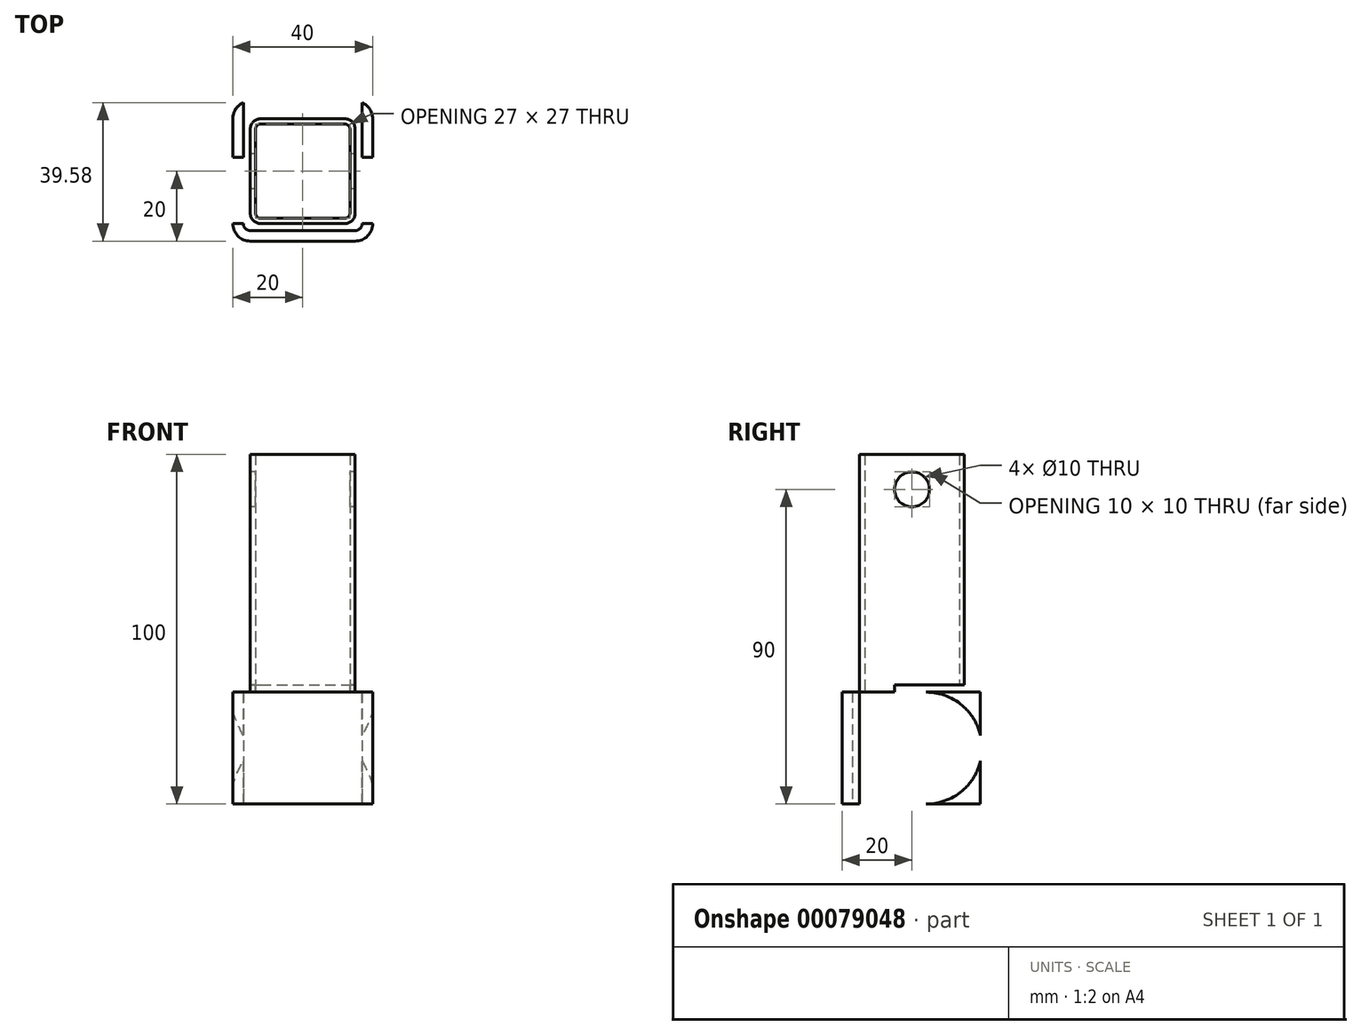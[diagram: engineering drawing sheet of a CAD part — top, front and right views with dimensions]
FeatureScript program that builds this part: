
annotation { "Feature Type Name" : "Feature", "Feature Type Description" : "" }
export const myFeature = defineFeature(function(context is Context, id is Id, definition is map)
    precondition{}
    {
        {
            var Q0;
            Q0=qCreatedBy(makeId("Top.planeOp"),FACE);
            var sketch = newSketch(context, id + "F0", { "sketchPlane" : qUnion([Q0])});
            skLineSegment(sketch, "E0.bottom", {"start": v(12, 15) * mm, "end": v(-12, 15) * mm});
            skLineSegment(sketch, "E0.top", {"start": v(12, -15) * mm, "end": v(-12, -15) * mm});
            skLineSegment(sketch, "E0.left", {"start": v(15, 12) * mm, "end": v(15, -12) * mm});
            skLineSegment(sketch, "E0.right", {"start": v(-15, 12) * mm, "end": v(-15, -12) * mm});
            skLineSegment(sketch, "E1", {"start": v(15, 15) * mm, "end": v(-15, -15) * mm, "construction": true});
            skPoint(sketch, "E2.visualSharp", {"position": v(15, 15) * mm});
            skArc(sketch, "E2.filletArc", {"start": v(15, 12) * mm, "mid": v(14.12, 14.12) * mm, "end": v(12, 15) * mm});
            skPoint(sketch, "E3.visualSharp", {"position": v(-15, 15) * mm});
            skArc(sketch, "E3.filletArc", {"start": v(-12, 15) * mm, "mid": v(-14.12, 14.12) * mm, "end": v(-15, 12) * mm});
            skPoint(sketch, "E4.visualSharp", {"position": v(-15, -15) * mm});
            skArc(sketch, "E4.filletArc", {"start": v(-15, -12) * mm, "mid": v(-14.12, -14.12) * mm, "end": v(-12, -15) * mm});
            skPoint(sketch, "E5.visualSharp", {"position": v(15, -15) * mm});
            skArc(sketch, "E5.filletArc", {"start": v(12, -15) * mm, "mid": v(14.12, -14.12) * mm, "end": v(15, -12) * mm});
            skArc(sketch, "E6.0", {"start": v(13.5, 12) * mm, "mid": v(13.06, 13.06) * mm, "end": v(12, 13.5) * mm});
            skLineSegment(sketch, "E6.1", {"start": v(12, 13.5) * mm, "end": v(-12, 13.5) * mm});
            skLineSegment(sketch, "E6.2", {"start": v(13.5, 12) * mm, "end": v(13.5, -12) * mm});
            skArc(sketch, "E6.3", {"start": v(-12, 13.5) * mm, "mid": v(-13.06, 13.06) * mm, "end": v(-13.5, 12) * mm});
            skArc(sketch, "E6.4", {"start": v(12, -13.5) * mm, "mid": v(13.06, -13.06) * mm, "end": v(13.5, -12) * mm});
            skLineSegment(sketch, "E6.5", {"start": v(12, -13.5) * mm, "end": v(-12, -13.5) * mm});
            skArc(sketch, "E6.6", {"start": v(-13.5, -12) * mm, "mid": v(-13.06, -13.06) * mm, "end": v(-12, -13.5) * mm});
            skLineSegment(sketch, "E6.7", {"start": v(-13.5, 12) * mm, "end": v(-13.5, -12) * mm});
            skSolve(sketch);
        }
        {
            var Q0;
            Q0=qCreatedBy(makeId("Top.planeOp"),FACE);
            var sketch = newSketch(context, id + "F1", { "sketchPlane" : qUnion([Q0])});
            skLineSegment(sketch, "E7.bottom", {"start": v(15, 20) * mm, "end": v(-15, 20) * mm});
            skLineSegment(sketch, "E7.top", {"start": v(15, -20) * mm, "end": v(-15, -20) * mm});
            skLineSegment(sketch, "E7.left", {"start": v(20, 15) * mm, "end": v(20, -15) * mm});
            skLineSegment(sketch, "E7.right", {"start": v(-20, 15) * mm, "end": v(-20, -15) * mm});
            skLineSegment(sketch, "E8", {"start": v(20, 20) * mm, "end": v(-20, -20) * mm, "construction": true});
            skPoint(sketch, "E9.visualSharp", {"position": v(20, 20) * mm});
            skArc(sketch, "E9.filletArc", {"start": v(20, 15) * mm, "mid": v(18.54, 18.54) * mm, "end": v(15, 20) * mm});
            skPoint(sketch, "E10.visualSharp", {"position": v(-20, 20) * mm});
            skArc(sketch, "E10.filletArc", {"start": v(-15, 20) * mm, "mid": v(-18.54, 18.54) * mm, "end": v(-20, 15) * mm});
            skPoint(sketch, "E11.visualSharp", {"position": v(-20, -20) * mm});
            skArc(sketch, "E11.filletArc", {"start": v(-20, -15) * mm, "mid": v(-18.54, -18.54) * mm, "end": v(-15, -20) * mm});
            skPoint(sketch, "E12.visualSharp", {"position": v(20, -20) * mm});
            skArc(sketch, "E12.filletArc", {"start": v(15, -20) * mm, "mid": v(18.54, -18.54) * mm, "end": v(20, -15) * mm});
            skArc(sketch, "E13.0", {"start": v(17, 15) * mm, "mid": v(16.41, 16.41) * mm, "end": v(15, 17) * mm});
            skLineSegment(sketch, "E13.1", {"start": v(15, 17) * mm, "end": v(-15, 17) * mm});
            skLineSegment(sketch, "E13.2", {"start": v(17, 15) * mm, "end": v(17, -15) * mm});
            skArc(sketch, "E13.3", {"start": v(-15, 17) * mm, "mid": v(-16.41, 16.41) * mm, "end": v(-17, 15) * mm});
            skArc(sketch, "E13.4", {"start": v(15, -17) * mm, "mid": v(16.41, -16.41) * mm, "end": v(17, -15) * mm});
            skLineSegment(sketch, "E13.5", {"start": v(15, -17) * mm, "end": v(-15, -17) * mm});
            skArc(sketch, "E13.6", {"start": v(-17, -15) * mm, "mid": v(-16.41, -16.41) * mm, "end": v(-15, -17) * mm});
            skLineSegment(sketch, "E13.7", {"start": v(-17, 15) * mm, "end": v(-17, -15) * mm});
            skSolve(sketch);
        }
        {
            var Q0;
            Q0 = qSketchRegion(id + "F0", true);
            extrude(context, id + "F2", {"entities" : qUnion([Q0]), "depth" : 100 * mm});
        }
        {
            var Q0;
            Q0 = qSketchRegion(id + "F0", true);
            extrude(context, id + "F3", {"entities" : qUnion([Q0]), "depth" : 100 * mm});
        }
        {
            var Q0;
            Q0=makeQuery(id+"F2.opExtrude","SWEPT_FACE",FACE,{"disambiguationData":[OSD([sQuery(id+"F0.wireOp",EDGE,"E0.right")])]});
            var sketch = newSketch(context, id + "F4", { "sketchPlane" : qUnion([Q0])});
            skLineSegment(sketch, "E14", {"start": v(0, 100) * mm, "end": v(0, 90) * mm, "construction": true});
            skPoint(sketch, "E14.endSnap0", {"position": v(0, 100) * mm});
            skCircle(sketch, "E15", {"center": v(0, 90) * mm, "radius": 5 * mm});
            skSolve(sketch);
        }
        {
            var Q0;
            Q0 = qSketchRegion(id + "F4", true);
            var Q1;
            Q1=sQuery(id+"F4.wireOp",EDGE,"E15");
            extrude(context, id + "F5", {"entities" : qUnion([Q0]), "operationType" : NewBodyOperationType.REMOVE, "surfaceEntities" : qUnion([Q1]), "endBound" : BoundingType.THROUGH_ALL, "oppositeDirection" : true, "depth" : 50 * mm});
        }
        {
            var Q0;
            Q0 = qSketchRegion(id + "F1", true);
            extrude(context, id + "F6", {"entities" : qUnion([Q0]), "depth" : 32 * mm});
        }
        {
            var Q0;
            Q0=makeQuery(id+"F6.opExtrude","SWEPT_FACE",FACE,{"disambiguationData":[OSD([sQuery(id+"F1.wireOp",EDGE,"E7.right")])]});
            var sketch = newSketch(context, id + "F7", { "sketchPlane" : qUnion([Q0])});
            skCircle(sketch, "E16", {"center": v(-4, 16) * mm, "radius": 5 * mm});
            skLineSegment(sketch, "E17", {"start": v(-4, 16) * mm, "end": v(15, 16) * mm, "construction": true});
            skPoint(sketch, "E17.endSnap0", {"position": v(15, 16) * mm});
            skLineSegment(sketch, "E18", {"start": v(0, 0) * mm, "end": v(0, 16) * mm, "construction": true});
            skLineSegment(sketch, "E19", {"start": v(-4, 0) * mm, "end": v(-4, 32) * mm, "construction": true});
            skSolve(sketch);
        }
        {
            var Q0;
            Q0=makeQuery(id+"F7.imprint","IMPRINT",FACE,{"disambiguationData":[TD([[makeQuery(id+"F7.imprint","IMPRINT",EDGE,{"derivedFrom":sQuery(id+"F7.wireOp",EDGE,"E16")}),1.0]])]});
            extrude(context, id + "F8", {"entities" : qUnion([Q0]), "operationType" : NewBodyOperationType.REMOVE, "endBound" : BoundingType.THROUGH_ALL, "oppositeDirection" : true, "depth" : 25 * mm});
        }
        {
            var Q0;
            Q0=makeQuery(id+"F6.opExtrude","SWEPT_FACE",FACE,{"disambiguationData":[OSD([sQuery(id+"F1.wireOp",EDGE,"E7.bottom")])]});
            var sketch = newSketch(context, id + "F9", { "sketchPlane" : qUnion([Q0])});
            skLineSegment(sketch, "E20.bottom", {"start": v(-17, 34.13) * mm, "end": v(17, 34.13) * mm});
            skLineSegment(sketch, "E20.top", {"start": v(-17, -2.13) * mm, "end": v(17, -2.13) * mm});
            skLineSegment(sketch, "E20.left", {"start": v(-17, 34.13) * mm, "end": v(-17, -2.13) * mm});
            skLineSegment(sketch, "E20.right", {"start": v(17, 34.13) * mm, "end": v(17, -2.13) * mm});
            skLineSegment(sketch, "E21", {"start": v(-15, 32) * mm, "end": v(15, 0) * mm, "construction": true});
            skLineSegment(sketch, "E22", {"start": v(0, -2.13) * mm, "end": v(0, 0) * mm, "construction": true});
            skSolve(sketch);
        }
        {
            var Q0;
            Q0=makeQuery(id+"F9.imprint","IMPRINT",FACE,{"disambiguationData":[TD([[makeQuery(id+"F9.imprint","IMPRINT",EDGE,{"derivedFrom":sQuery(id+"F9.wireOp",EDGE,"E20.bottom")}),-1.0]])]});
            var Q1;
            {var subQ0=sQuery(id+"F1.wireOp",EDGE,"E7.bottom");Q1=makeQuery(id+"F9.imprint","IMPRINT",FACE,{"disambiguationData":[TD([[makeQuery(id+"F9.imprint","IMPRINT",EDGE,{"derivedFrom":makeQuery(id+"F6.opExtrude","CAP_EDGE",EDGE,{"disambiguationData":[OSD([subQ0])],"isStart":true})}),1.0]])]});}
            extrude(context, id + "F10", {"entities" : qUnion([Q0, Q1]), "operationType" : NewBodyOperationType.REMOVE, "oppositeDirection" : true, "depth" : 25 * mm});
        }
        {
            var Q0;
            Q0=makeQuery(id+"F10.boolean.opBoolean","MERGE",FACE,{"derivedFrom":[makeQuery(id+"F6.opExtrude","SWEPT_FACE",FACE,{"disambiguationData":[OSD([sQuery(id+"F1.wireOp",EDGE,"E13.7")])]}),makeQuery(id+"F10.opExtrude","SWEPT_FACE",FACE,{"disambiguationData":[OSD([sQuery(id+"F9.wireOp",EDGE,"E20.right")])]})]});
            var sketch = newSketch(context, id + "F11", { "sketchPlane" : qUnion([Q0])});
            skArc(sketch, "E23", {"start": v(4, 32) * mm, "mid": v(20, 16) * mm, "end": v(4, 0) * mm});
            skLineSegment(sketch, "E24", {"start": v(4, 32) * mm, "end": v(4, 0) * mm, "construction": true});
            skSolve(sketch);
        }
        {
            var Q0;
            {var subQ0=sQuery(id+"F11.wireOp",EDGE,"E23");var subQ1=makeQuery(id+"F10.opExtrude","SWEPT_FACE",FACE,{"disambiguationData":[OSD([sQuery(id+"F9.wireOp",EDGE,"E20.right")])]});var subQ2=sQuery(id+"F1.wireOp",EDGE,"E10.filletArc");var subQ5=makeQuery(id+"F10.boolean.opBoolean","INTERSECT",EDGE,{"derivedFrom":[makeQuery(id+"F6.opExtrude","SWEPT_FACE",FACE,{"disambiguationData":[OSD([subQ2])]}),subQ1]});var subQ6=makeQuery(id+"F11.imprint","INTERSECT",VERTEX,{"disambiguationData":[OD(0.0)],"derivedFrom":[subQ5,subQ0]});Q0=makeQuery(id+"F11.imprint","IMPRINT",FACE,{"disambiguationData":[TD([[makeQuery(id+"F11.imprint","IMPRINT",EDGE,{"disambiguationData":[TD([[subQ6,1.0]])],"derivedFrom":subQ0}),1.0]])]});}
            var Q1;
            {var subQ0=sQuery(id+"F11.wireOp",EDGE,"E23");var subQ1=makeQuery(id+"F10.opExtrude","SWEPT_FACE",FACE,{"disambiguationData":[OSD([sQuery(id+"F9.wireOp",EDGE,"E20.right")])]});var subQ2=sQuery(id+"F1.wireOp",EDGE,"E10.filletArc");var subQ5=makeQuery(id+"F10.boolean.opBoolean","INTERSECT",EDGE,{"derivedFrom":[makeQuery(id+"F6.opExtrude","SWEPT_FACE",FACE,{"disambiguationData":[OSD([subQ2])]}),subQ1]});var subQ6=makeQuery(id+"F11.imprint","INTERSECT",VERTEX,{"disambiguationData":[OD(1.0)],"derivedFrom":[subQ5,subQ0]});Q1=makeQuery(id+"F11.imprint","IMPRINT",FACE,{"disambiguationData":[TD([[makeQuery(id+"F11.imprint","IMPRINT",EDGE,{"disambiguationData":[TD([[subQ6,-1.0]])],"derivedFrom":subQ0}),1.0]])]});}
            extrude(context, id + "F12", {"entities" : qUnion([Q0, Q1]), "operationType" : NewBodyOperationType.REMOVE, "oppositeDirection" : true, "depth" : 100 * mm, "symmetric" : true});
        }
    });
